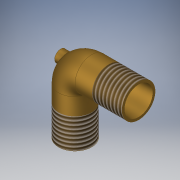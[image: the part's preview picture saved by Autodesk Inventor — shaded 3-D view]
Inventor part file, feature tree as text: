
AUTODESK INVENTOR PART (.ipt)
format: ipt  version: 2018 (Build 220112000, 112)  size: 788,992 bytes
history: native  units: in
note: dims shown in document units (in); Inventor stores cm internally (conversion verified against a paired STEP export)
features: sketch x7, extrude x6, other x3, plane x3, thread x2, chamfer x1
ambient origin geometry x8: Origin, YZ Plane, XZ Plane, XY Plane, X Axis, Y Axis, Z Axis, Center Point
bodies: Body1 (feature_tree)
feature tree (22):
  extrude  "Extrusion5"  Depth=0.5515in
  other  "Bend Part2"
  thread  "Thread3"  [1 undecoded]
  thread  "Thread4"  [1 undecoded]
  plane  "Work Plane3"
  extrude  "Extrusion6"  Depth=0.276in TaperAngle=90.0deg
  plane  "Work Plane4"
  extrude  "Extrusion7"  Depth=0.5in TaperAngle=0.0deg
  chamfer  "Chamfer2"  Distance=29.5276in Angle=360.0deg
  plane  "Work Plane5"
  extrude  "Extrusion8"  TaperAngle=0.0deg  [1 undecoded]
  extrude  "Extrusion9"  Depth=0.285in TaperAngle=45.0deg
  extrude  "Extrusion10"  TaperAngle=0.0deg  [1 undecoded]
  other  "Work Axis1"
  other  "Work Axis2"
  sketch  "Sketch6"  dims[d24=0.475in d25=0.5515in d26=2.0in d27=0.0in d28=2.0in]
  sketch  "Sketch7"  dims[d29=1.0in d30=0.276in d31=90.0deg]
  sketch  "Sketch8"  dims[d32=0.5in d33=0.0in d34=0.5in d35=0.0in]
  sketch  "Sketch9"  dims[d36=-0.45in]
  sketch  "Sketch10"  dims[d37=0.46in d38=29.5276in d40=360.0deg]
  sketch  "Sketch11"  dims[d42=0.45in d43=0.0in d44=0.0in]
  sketch  "Sketch12"  dims[d45=0.1in d46=0.0in d47=0.0925in d48=0.125in d49=45.0deg d50=0.0in d51=0.2in d52=0.3in d53=0.0in d54=0.075in d55=0.3in d56=0.0in d57=0.19in d58=0.285in d59=0.0in]
note: 4 required parameter values undecoded (feature->parameter linkage not recoverable at this tier; creation-order binding heuristic only, values carry confidence <= 0.55)
